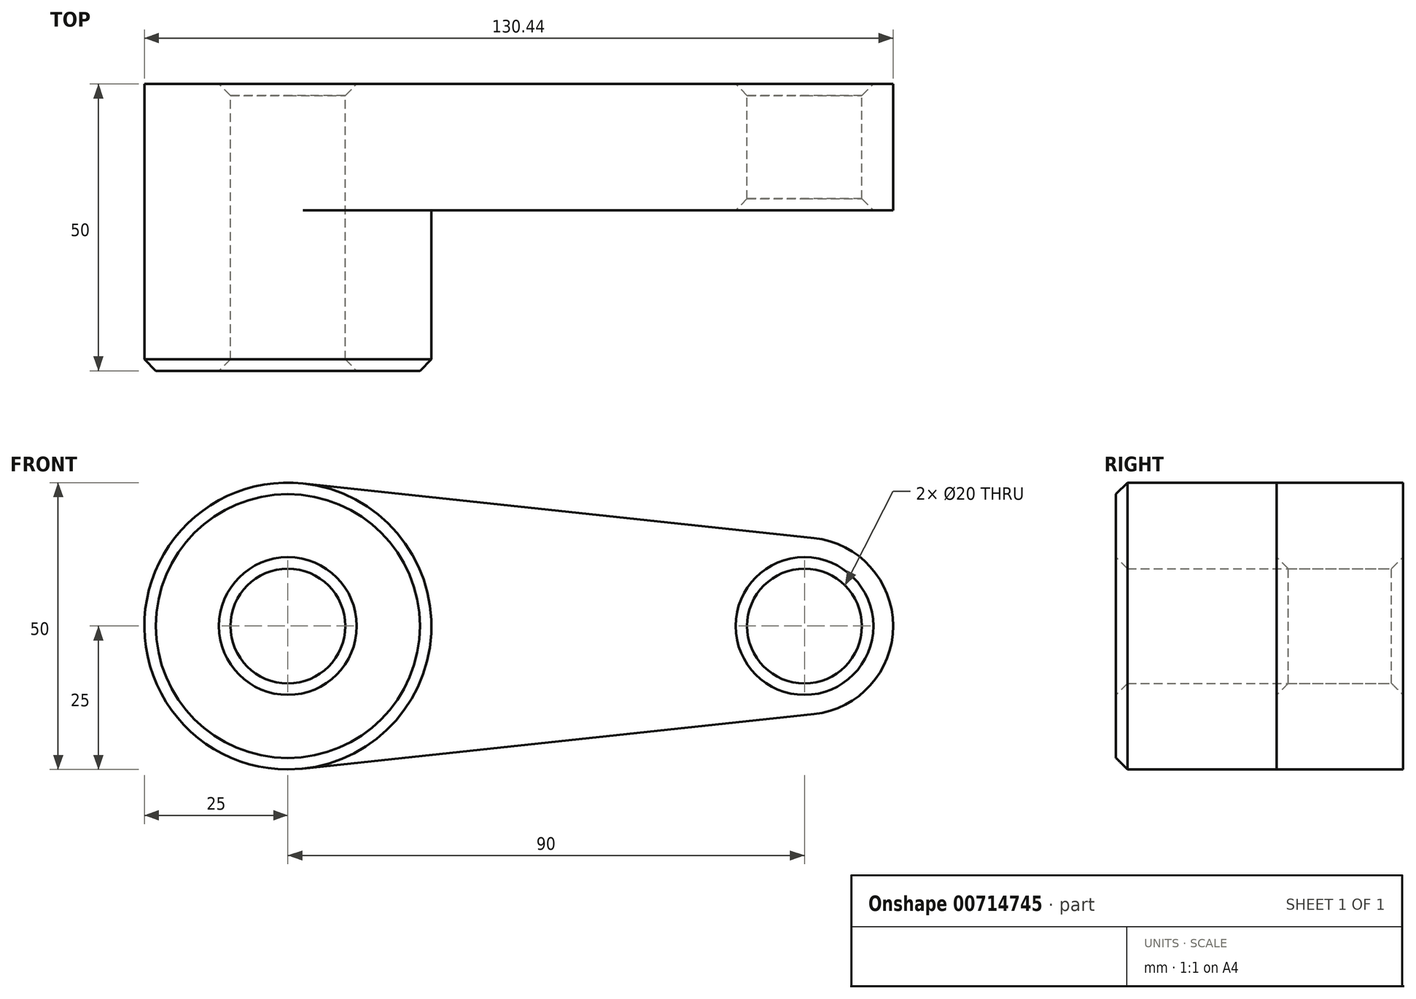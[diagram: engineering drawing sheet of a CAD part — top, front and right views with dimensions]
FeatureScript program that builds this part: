
annotation { "Feature Type Name" : "Feature", "Feature Type Description" : "" }
export const myFeature = defineFeature(function(context is Context, id is Id, definition is map)
    precondition{}
    {
        {
            var Q0;
            Q0=qCreatedBy(makeId("Front.planeOp"),FACE);
            var sketch = newSketch(context, id + "F0", { "sketchPlane" : qUnion([Q0])});
            skCircle(sketch, "E0", {"center": v(0, 0) * mm, "radius": 25 * mm});
            skCircle(sketch, "E1", {"center": v(90, 0) * mm, "radius": 15.44 * mm});
            skLineSegment(sketch, "E2", {"start": v(2.66, 24.86) * mm, "end": v(91.64, 15.35) * mm});
            skCircle(sketch, "E3", {"center": v(0, 0) * mm, "radius": 10 * mm});
            skCircle(sketch, "E4", {"center": v(90, 0) * mm, "radius": 10 * mm});
            skLineSegment(sketch, "E5", {"start": v(2.66, -24.86) * mm, "end": v(91.64, -15.35) * mm});
            skSolve(sketch);
        }
        {
            var Q0;
            Q0 = qSketchRegion(id + "F0", true);
            var sketch = newSketch(context, id + "F1", { "sketchPlane" : qUnion([Q0])});
            skSolve(sketch);
        }
        {
            var Q0;
            Q0 = qSketchRegion(id + "F0", true);
            var Q1;
            Q1 = qSketchRegion(id + "F1", true);
            extrude(context, id + "F2", {"entities" : qUnion([Q0, Q1]), "depth" : 22 * mm, "offsetDistance" : 25 * mm});
        }
        {
            var Q0;
            Q0=makeQuery(id+"F0.imprint","IMPRINT",FACE,{"disambiguationData":[TD([[makeQuery(id+"F0.imprint","IMPRINT",EDGE,{"derivedFrom":sQuery(id+"F0.wireOp",EDGE,"E3")}),-1.0]])]});
            extrude(context, id + "F3", {"entities" : qUnion([Q0]), "operationType" : NewBodyOperationType.ADD, "depth" : 50 * mm, "offsetDistance" : 25 * mm});
        }
        {
            var Q0;
            Q0=makeQuery(id+"F2.opExtrude","CAP_EDGE",EDGE,{"disambiguationData":[OSD([sQuery(id+"F0.wireOp",EDGE,"E4")])],"isStart":false});
            var Q1;
            Q1=makeQuery(id+"F3.opExtrude","CAP_EDGE",EDGE,{"disambiguationData":[OSD([sQuery(id+"F0.wireOp",EDGE,"E3")])],"isStart":false});
            var Q2;
            Q2=makeQuery(id+"F3.opExtrude","CAP_EDGE",EDGE,{"disambiguationData":[OSD([sQuery(id+"F0.wireOp",EDGE,"E0")])],"isStart":false});
            var Q3;
            Q3=makeQuery(id+"F2.opExtrude","CAP_EDGE",EDGE,{"disambiguationData":[OSD([sQuery(id+"F0.wireOp",EDGE,"E4")])],"isStart":true});
            var Q4;
            Q4=makeQuery(id+"F2.opExtrude","CAP_EDGE",EDGE,{"disambiguationData":[OSD([sQuery(id+"F0.wireOp",EDGE,"E3")])],"isStart":true});
            chamfer(context, id + "F4", {"entities" : qUnion([Q0, Q1, Q2, Q3, Q4]), "width" : 2 * mm, "tangentPropagation" : true});
        }
    });
